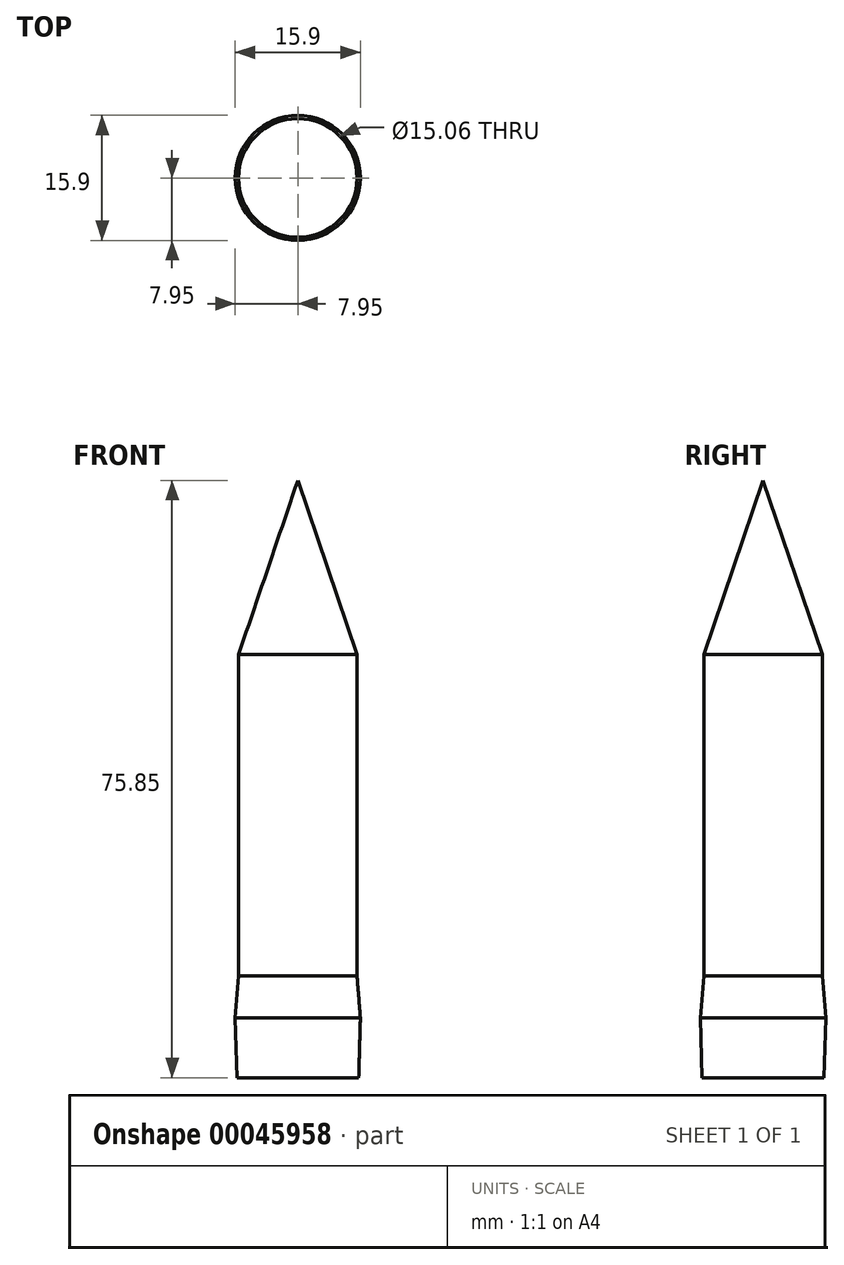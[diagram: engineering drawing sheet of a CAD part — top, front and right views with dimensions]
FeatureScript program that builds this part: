
annotation { "Feature Type Name" : "Feature", "Feature Type Description" : "" }
export const myFeature = defineFeature(function(context is Context, id is Id, definition is map)
    precondition{}
    {
        {
            var Q0;
            Q0=qCreatedBy(makeId("Front.planeOp"),FACE);
            var sketch = newSketch(context, id + "F0", { "sketchPlane" : qUnion([Q0])});
            skLineSegment(sketch, "E0", {"start": v(-7.58, 0) * mm, "end": v(0, 0) * mm});
            skLineSegment(sketch, "E1", {"start": v(0, 0) * mm, "end": v(0, 75.68) * mm});
            skSolve(sketch);
        }
        {
            var Q0;
            Q0=qCreatedBy(makeId("Front.planeOp"),FACE);
            var sketch = newSketch(context, id + "F1", { "sketchPlane" : qUnion([Q0])});
            skLineSegment(sketch, "E2", {"start": v(-7.74, 0) * mm, "end": v(-7.95, 7.57) * mm});
            skLineSegment(sketch, "E3", {"start": v(-7.53, 12.92) * mm, "end": v(-7.95, 7.57) * mm});
            skLineSegment(sketch, "E4", {"start": v(-7.53, 12.92) * mm, "end": v(-7.53, 53.73) * mm});
            skLineSegment(sketch, "E5", {"start": v(-7.53, 53.73) * mm, "end": v(0, 75.85) * mm});
            skSolve(sketch);
        }
        {
            var Q0;
            Q0=sQuery(id+"F1.wireOp",EDGE,"E5");
            var Q1;
            Q1=sQuery(id+"F1.wireOp",EDGE,"E4");
            var Q2;
            Q2=sQuery(id+"F1.wireOp",EDGE,"E3");
            var Q3;
            Q3=sQuery(id+"F1.wireOp",EDGE,"E2");
            var Q4;
            Q4=sQuery(id+"F0.wireOp",EDGE,"E1");
            revolve(context, id + "F2", {"bodyType" : ToolBodyType.SURFACE, "surfaceEntities" : qUnion([Q0, Q1, Q2, Q3]), "axis" : qUnion([Q4]), "revolveType" : RevolveType.FULL});
        }
    });
